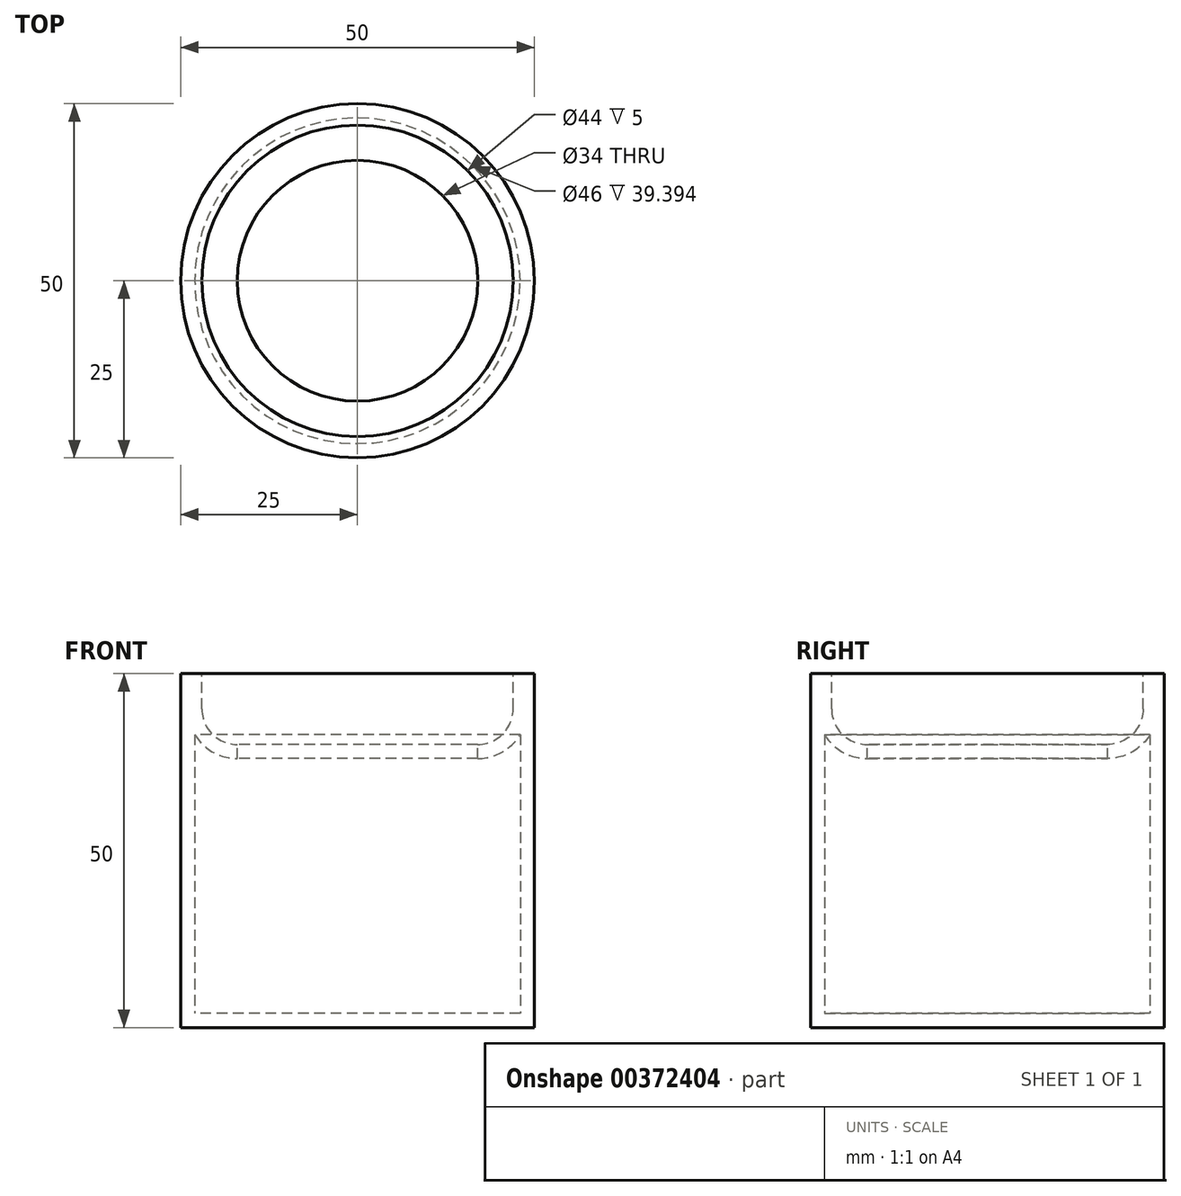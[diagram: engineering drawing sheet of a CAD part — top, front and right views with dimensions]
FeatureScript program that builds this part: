
annotation { "Feature Type Name" : "Feature", "Feature Type Description" : "" }
export const myFeature = defineFeature(function(context is Context, id is Id, definition is map)
    precondition{}
    {
        {
            var Q0;
            Q0=qCreatedBy(makeId("Top.planeOp"),FACE);
            var sketch = newSketch(context, id + "F0", { "sketchPlane" : qUnion([Q0])});
            skCircle(sketch, "E0", {"center": v(0, 0) * mm, "radius": 25 * mm});
            skSolve(sketch);
        }
        {
            var Q0;
            Q0=makeQuery(id+"F0.imprint","IMPRINT",FACE,{"disambiguationData":[TD([[makeQuery(id+"F0.imprint","IMPRINT",EDGE,{"derivedFrom":sQuery(id+"F0.wireOp",EDGE,"E0")}),1.0]])]});
            extrude(context, id + "F1", {"entities" : qUnion([Q0]), "depth" : 50 * mm});
        }
        {
            var Q0;
            Q0=makeQuery(id+"F1.opExtrude","CAP_FACE",FACE,{"disambiguationData":[OSD([sQuery(id+"F0.wireOp",EDGE,"E0")])],"isStart":false});
            var sketch = newSketch(context, id + "F2", { "sketchPlane" : qUnion([Q0])});
            skCircle(sketch, "E1", {"center": v(0, 0) * mm, "radius": 22 * mm});
            skSolve(sketch);
        }
        {
            var Q0;
            Q0 = qSketchRegion(id + "F2", true);
            extrude(context, id + "F3", {"entities" : qUnion([Q0]), "operationType" : NewBodyOperationType.REMOVE, "oppositeDirection" : true, "depth" : 10 * mm});
        }
        {
            var Q0;
            Q0=makeQuery(id+"F3.boolean.opBoolean","COPY",EDGE,{"derivedFrom":makeQuery(id+"F3.opExtrude","CAP_EDGE",EDGE,{"disambiguationData":[OSD([sQuery(id+"F2.wireOp",EDGE,"E1")])],"isStart":false})});
            fillet(context, id + "F4", {"entities" : qUnion([Q0]), "radius" : 5 * mm, "tangentPropagation" : true, "allowEdgeOverflow" : false});
        }
        {
            var Q0;
            Q0=makeQuery(id+"F3.boolean.opBoolean","COPY",FACE,{"derivedFrom":makeQuery(id+"F3.opExtrude","CAP_FACE",FACE,{"disambiguationData":[OSD([sQuery(id+"F2.wireOp",EDGE,"E1")])],"isStart":false})});
            shell(context, id + "F5", {"entities" : qUnion([Q0]), "thickness" : 2 * mm});
        }
    });
